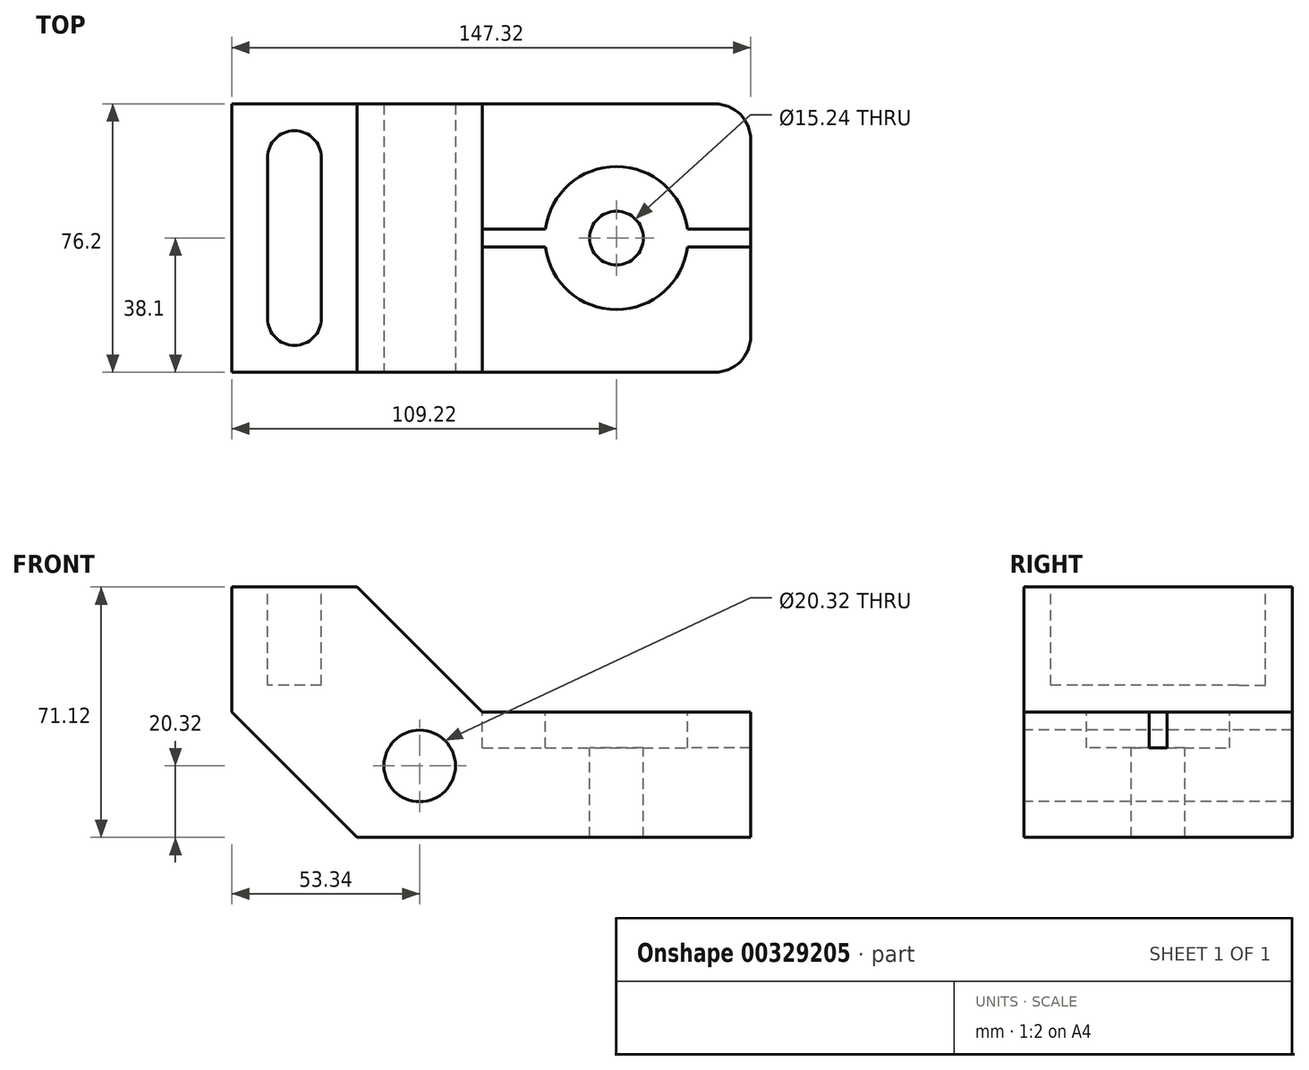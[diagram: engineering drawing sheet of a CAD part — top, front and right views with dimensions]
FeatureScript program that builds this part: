
annotation { "Feature Type Name" : "Feature", "Feature Type Description" : "" }
export const myFeature = defineFeature(function(context is Context, id is Id, definition is map)
    precondition{}
    {
        {
            var Q0;
            Q0=qCreatedBy(makeId("Front.planeOp"),FACE);
            var sketch = newSketch(context, id + "F0", { "sketchPlane" : qUnion([Q0])});
            skLineSegment(sketch, "E0", {"start": v(0, 0) * mm, "end": v(-35.56, 35.56) * mm});
            skLineSegment(sketch, "E1", {"start": v(-35.56, 35.56) * mm, "end": v(-35.56, 71.12) * mm});
            skLineSegment(sketch, "E2", {"start": v(-35.56, 71.12) * mm, "end": v(0, 71.12) * mm});
            skLineSegment(sketch, "E3", {"start": v(0, 71.12) * mm, "end": v(35.56, 35.56) * mm});
            skLineSegment(sketch, "E4", {"start": v(35.56, 35.56) * mm, "end": v(111.76, 35.56) * mm});
            skLineSegment(sketch, "E5", {"start": v(111.76, 35.56) * mm, "end": v(111.76, 0) * mm});
            skLineSegment(sketch, "E6", {"start": v(111.76, 0) * mm, "end": v(0, 0) * mm});
            skSolve(sketch);
        }
        {
            var Q0;
            Q0 = qSketchRegion(id + "F0", true);
            extrude(context, id + "F1", {"entities" : qUnion([Q0]), "depth" : 76.2 * mm});
        }
        {
            var Q0;
            Q0=makeQuery(id+"F1.opExtrude","CAP_EDGE",EDGE,{"disambiguationData":[OSD([sQuery(id+"F0.wireOp",EDGE,"E5")])],"isStart":false});
            var Q1;
            Q1=makeQuery(id+"F1.opExtrude","CAP_EDGE",EDGE,{"disambiguationData":[OSD([sQuery(id+"F0.wireOp",EDGE,"E5")])],"isStart":true});
            fillet(context, id + "F2", {"entities" : qUnion([Q0, Q1]), "radius" : 10.16 * mm, "tangentPropagation" : true, "allowEdgeOverflow" : false});
        }
        {
            var Q0;
            Q0=makeQuery(id+"F1.opExtrude","CAP_FACE",FACE,{"disambiguationData":[OSD([sQuery(id+"F0.wireOp",EDGE,"E0"),sQuery(id+"F0.wireOp",EDGE,"E1"),sQuery(id+"F0.wireOp",EDGE,"E2"),sQuery(id+"F0.wireOp",EDGE,"E3"),sQuery(id+"F0.wireOp",EDGE,"E4"),sQuery(id+"F0.wireOp",EDGE,"E5"),sQuery(id+"F0.wireOp",EDGE,"E6")])],"isStart":false});
            var sketch = newSketch(context, id + "F3", { "sketchPlane" : qUnion([Q0])});
            skCircle(sketch, "E7", {"center": v(17.78, 20.32) * mm, "radius": 10.16 * mm});
            skSolve(sketch);
        }
        {
            var Q0;
            Q0 = qSketchRegion(id + "F3", true);
            extrude(context, id + "F4", {"entities" : qUnion([Q0]), "operationType" : NewBodyOperationType.REMOVE, "endBound" : BoundingType.THROUGH_ALL, "oppositeDirection" : true, "depth" : 25.4 * mm});
        }
        {
            var Q0;
            Q0=makeQuery(id+"F1.opExtrude","SWEPT_FACE",FACE,{"disambiguationData":[OSD([sQuery(id+"F0.wireOp",EDGE,"E2")])]});
            var sketch = newSketch(context, id + "F5", { "sketchPlane" : qUnion([Q0])});
            skArc(sketch, "E8", {"start": v(-10.16, -15.24) * mm, "mid": v(-17.78, -7.62) * mm, "end": v(-25.4, -15.24) * mm});
            skArc(sketch, "E9", {"start": v(-25.4, -60.96) * mm, "mid": v(-17.78, -68.58) * mm, "end": v(-10.16, -60.96) * mm});
            skLineSegment(sketch, "E10", {"start": v(-25.4, -15.24) * mm, "end": v(-25.4, -60.96) * mm});
            skLineSegment(sketch, "E11", {"start": v(-10.16, -60.96) * mm, "end": v(-10.16, -15.24) * mm});
            skSolve(sketch);
        }
        {
            var Q0;
            Q0 = qSketchRegion(id + "F5", true);
            extrude(context, id + "F6", {"entities" : qUnion([Q0]), "operationType" : NewBodyOperationType.REMOVE, "oppositeDirection" : true, "depth" : 27.94 * mm});
        }
        {
            var Q0;
            Q0=makeQuery(id+"F1.opExtrude","SWEPT_FACE",FACE,{"disambiguationData":[OSD([sQuery(id+"F0.wireOp",EDGE,"E4")])]});
            var sketch = newSketch(context, id + "F7", { "sketchPlane" : qUnion([Q0])});
            skCircle(sketch, "E12", {"center": v(73.66, -38.1) * mm, "radius": 20.32 * mm});
            skLineSegment(sketch, "E13", {"start": v(93.82, -35.56) * mm, "end": v(111.76, -35.56) * mm});
            skLineSegment(sketch, "E14", {"start": v(111.76, -35.56) * mm, "end": v(111.76, -40.64) * mm});
            skLineSegment(sketch, "E15", {"start": v(111.76, -40.64) * mm, "end": v(93.82, -40.64) * mm});
            skLineSegment(sketch, "E16", {"start": v(53.5, -35.56) * mm, "end": v(35.56, -35.56) * mm});
            skLineSegment(sketch, "E17", {"start": v(35.56, -35.56) * mm, "end": v(35.56, -40.64) * mm});
            skLineSegment(sketch, "E18", {"start": v(35.56, -40.64) * mm, "end": v(53.5, -40.64) * mm});
            skLineSegment(sketch, "E19", {"start": v(35.56, -38.1) * mm, "end": v(111.76, -38.1) * mm, "construction": true});
            skSolve(sketch);
        }
        {
            var Q0;
            Q0 = qSketchRegion(id + "F7", true);
            extrude(context, id + "F8", {"entities" : qUnion([Q0]), "operationType" : NewBodyOperationType.REMOVE, "oppositeDirection" : true, "depth" : 10.16 * mm});
        }
        {
            var Q0;
            Q0=makeQuery(id+"F8.boolean.opBoolean","COPY",FACE,{"derivedFrom":makeQuery(id+"F8.opExtrude","CAP_FACE",FACE,{"disambiguationData":[OSD([sQuery(id+"F7.wireOp",EDGE,"E12"),sQuery(id+"F7.wireOp",EDGE,"E13"),sQuery(id+"F7.wireOp",EDGE,"E14"),sQuery(id+"F7.wireOp",EDGE,"E15"),sQuery(id+"F7.wireOp",EDGE,"E16"),sQuery(id+"F7.wireOp",EDGE,"E17"),sQuery(id+"F7.wireOp",EDGE,"E18")])],"isStart":false})});
            var sketch = newSketch(context, id + "F9", { "sketchPlane" : qUnion([Q0])});
            skCircle(sketch, "E20", {"center": v(73.66, -38.1) * mm, "radius": 7.62 * mm});
            skSolve(sketch);
        }
        {
            var Q0;
            Q0 = qSketchRegion(id + "F9", true);
            extrude(context, id + "F10", {"entities" : qUnion([Q0]), "operationType" : NewBodyOperationType.REMOVE, "endBound" : BoundingType.THROUGH_ALL, "oppositeDirection" : true, "depth" : 25.4 * mm});
        }
    });
